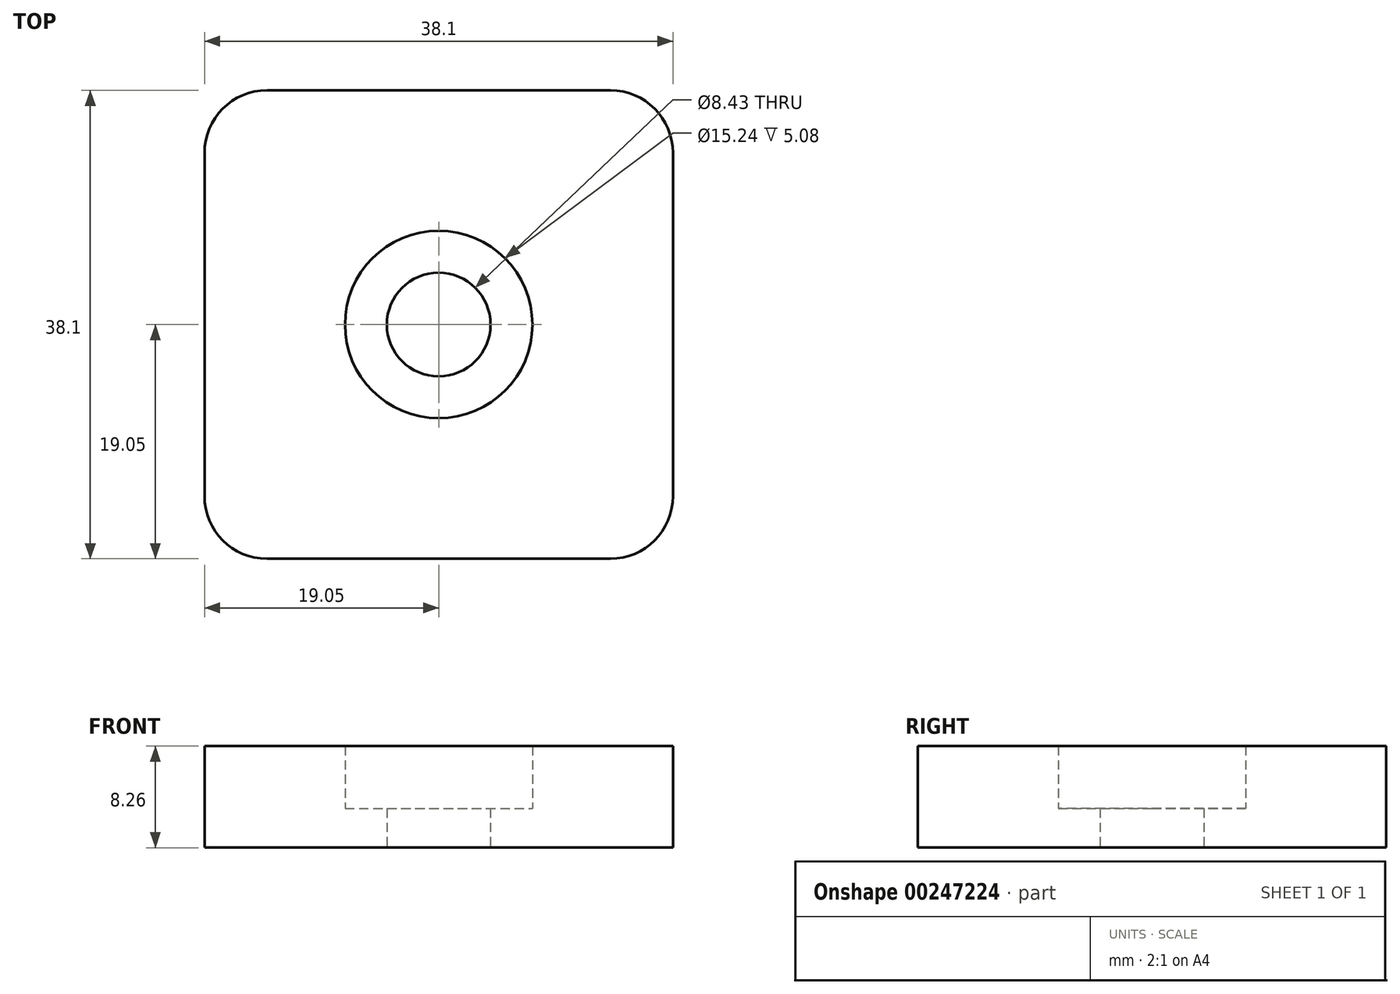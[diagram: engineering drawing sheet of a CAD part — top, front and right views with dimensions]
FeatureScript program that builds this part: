
annotation { "Feature Type Name" : "Feature", "Feature Type Description" : "" }
export const myFeature = defineFeature(function(context is Context, id is Id, definition is map)
    precondition{}
    {
        {
            var Q0;
            Q0=qCreatedBy(makeId("Top.planeOp"),FACE);
            var sketch = newSketch(context, id + "F0", { "sketchPlane" : qUnion([Q0])});
            skLineSegment(sketch, "E0.bottom", {"start": v(19.05, -19.05) * mm, "end": v(-19.05, -19.05) * mm});
            skLineSegment(sketch, "E0.top", {"start": v(19.05, 19.05) * mm, "end": v(-19.05, 19.05) * mm});
            skLineSegment(sketch, "E0.left", {"start": v(19.05, -19.05) * mm, "end": v(19.05, 19.05) * mm});
            skLineSegment(sketch, "E0.right", {"start": v(-19.05, -19.05) * mm, "end": v(-19.05, 19.05) * mm});
            skPoint(sketch, "E0.middle", {"position": v(0, 0) * mm});
            skSolve(sketch);
        }
        {
            var Q0;
            Q0 = qSketchRegion(id + "F0", true);
            extrude(context, id + "F1", {"entities" : qUnion([Q0]), "oppositeDirection" : true, "depth" : 8.25 * mm});
        }
        {
            var Q0;
            Q0=makeQuery(id+"F1.opExtrude","SWEPT_EDGE",EDGE,{"disambiguationData":[OSD([sQuery(id+"F0.wireOp",EDGE,"E0.top"),sQuery(id+"F0.wireOp",EDGE,"E0.right")])]});
            var Q1;
            Q1=makeQuery(id+"F1.opExtrude","SWEPT_EDGE",EDGE,{"disambiguationData":[OSD([sQuery(id+"F0.wireOp",EDGE,"E0.bottom"),sQuery(id+"F0.wireOp",EDGE,"E0.right")])]});
            var Q2;
            Q2=makeQuery(id+"F1.opExtrude","SWEPT_EDGE",EDGE,{"disambiguationData":[OSD([sQuery(id+"F0.wireOp",EDGE,"E0.bottom"),sQuery(id+"F0.wireOp",EDGE,"E0.left")])]});
            var Q3;
            Q3=makeQuery(id+"F1.opExtrude","SWEPT_EDGE",EDGE,{"disambiguationData":[OSD([sQuery(id+"F0.wireOp",EDGE,"E0.top"),sQuery(id+"F0.wireOp",EDGE,"E0.left")])]});
            fillet(context, id + "F2", {"entities" : qUnion([Q0, Q1, Q2, Q3]), "radius" : 5.08 * mm, "tangentPropagation" : true, "allowEdgeOverflow" : false});
        }
        {
            var Q0;
            Q0=sQuery(id+"F0.wireOp",VERTEX,"E0.middle");
            var Q1;
            Q1=makeQuery(id+"F1.opExtrude","SWEPT_BODY",BODY,{"disambiguationData":[OSD([sQuery(id+"F0.wireOp",EDGE,"E0.bottom"),sQuery(id+"F0.wireOp",EDGE,"E0.top"),sQuery(id+"F0.wireOp",EDGE,"E0.left"),sQuery(id+"F0.wireOp",EDGE,"E0.right")])]});
            hole(context, id + "F3", {"style" : HoleStyle.C_BORE, "endStyle" : HoleEndStyle.THROUGH, "holeDiameter" : 8.43 * mm, "cBoreDiameter" : 15.24 * mm, "cBoreDepth" : 5.08 * mm, "tappedDepth" : 12.7 * mm, "tapClearance" : 3, "locations" : qUnion([Q0]), "scope" : qUnion([Q1]), "startStyle" : HoleStartStyle.PART});
        }
    });
